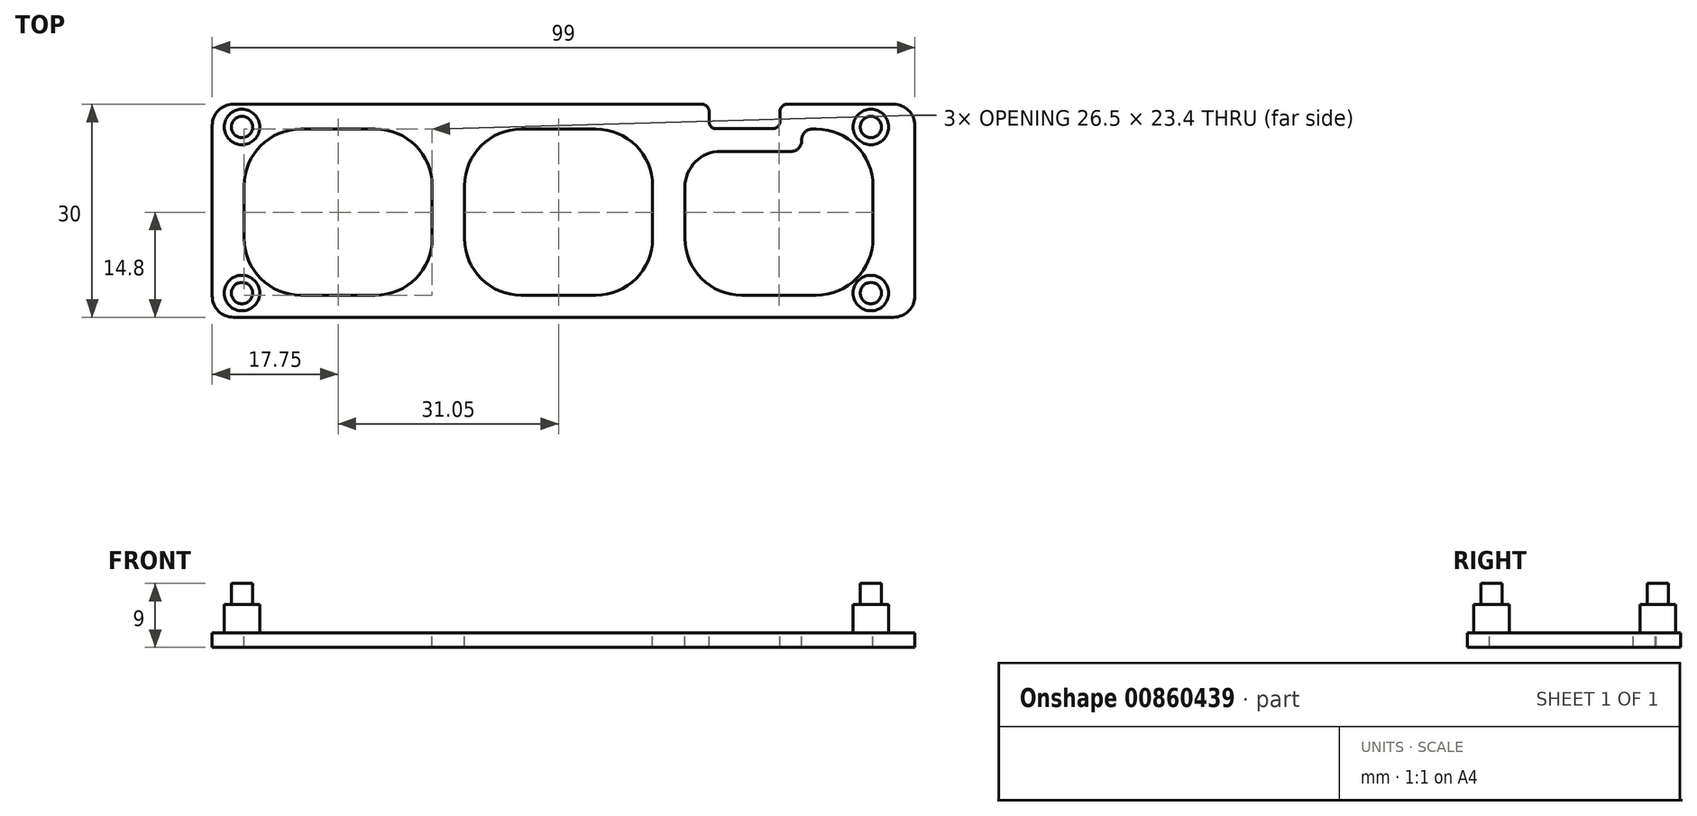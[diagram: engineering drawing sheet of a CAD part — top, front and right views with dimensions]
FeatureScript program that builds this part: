
annotation { "Feature Type Name" : "Feature", "Feature Type Description" : "" }
export const myFeature = defineFeature(function(context is Context, id is Id, definition is map)
    precondition{}
    {
        {
            var Q0;
            Q0=qCreatedBy(makeId("Top.planeOp"),FACE);
            var sketch = newSketch(context, id + "F0", { "sketchPlane" : qUnion([Q0])});
            skLineSegment(sketch, "E0.top", {"start": v(70, -3.43) * mm, "end": v(80, -3.43) * mm});
            skLineSegment(sketch, "E0.left", {"start": v(70, 0) * mm, "end": v(70, -3.43) * mm});
            skLineSegment(sketch, "E0.right", {"start": v(80, 0) * mm, "end": v(80, -3.43) * mm});
            skPoint(sketch, "E1.left.start.orphan", {"position": v(0, 0) * mm});
            skLineSegment(sketch, "E2.bottom", {"start": v(0, 0) * mm, "end": v(70, 0) * mm});
            skLineSegment(sketch, "E2.top", {"start": v(0, -30) * mm, "end": v(99, -30) * mm});
            skLineSegment(sketch, "E2.left", {"start": v(0, 0) * mm, "end": v(0, -30) * mm});
            skLineSegment(sketch, "E2.right", {"start": v(99, 0) * mm, "end": v(99, -30) * mm});
            skLineSegment(sketch, "E3.trimOffspring", {"start": v(80, 0) * mm, "end": v(99, 0) * mm});
            skLineSegment(sketch, "E4.bottom", {"start": v(0, 0) * mm, "end": v(4.5, 0) * mm, "construction": true});
            skLineSegment(sketch, "E4.top", {"start": v(0, -3.5) * mm, "end": v(4.5, -3.5) * mm, "construction": true});
            skLineSegment(sketch, "E4.left", {"start": v(0, 0) * mm, "end": v(0, -3.5) * mm, "construction": true});
            skLineSegment(sketch, "E4.right", {"start": v(4.5, 0) * mm, "end": v(4.5, -3.5) * mm, "construction": true});
            skLineSegment(sketch, "E5.bottom", {"start": v(4.5, -3.5) * mm, "end": v(66.6, -3.5) * mm, "construction": true});
            skLineSegment(sketch, "E5.top", {"start": v(4.5, -26.9) * mm, "end": v(93.1, -26.9) * mm, "construction": true});
            skLineSegment(sketch, "E5.left", {"start": v(4.5, -3.5) * mm, "end": v(4.5, -26.9) * mm, "construction": true});
            skLineSegment(sketch, "E5.right", {"start": v(93.1, -3.5) * mm, "end": v(93.1, -26.9) * mm, "construction": true});
            skLineSegment(sketch, "E6.bottom", {"start": v(12.5, -3.5) * mm, "end": v(23, -3.5) * mm});
            skLineSegment(sketch, "E6.top", {"start": v(12.5, -26.9) * mm, "end": v(23, -26.9) * mm});
            skLineSegment(sketch, "E6.left", {"start": v(4.5, -11.5) * mm, "end": v(4.5, -18.9) * mm});
            skLineSegment(sketch, "E6.right", {"start": v(31, -11.5) * mm, "end": v(31, -18.9) * mm});
            skLineSegment(sketch, "E7.bottom", {"start": v(85.1, -3.5) * mm, "end": v(84.55, -3.5) * mm});
            skLineSegment(sketch, "E7.top", {"start": v(85.1, -26.9) * mm, "end": v(74.6, -26.9) * mm});
            skLineSegment(sketch, "E7.left", {"start": v(93.1, -11.5) * mm, "end": v(93.1, -18.9) * mm});
            skLineSegment(sketch, "E7.right", {"start": v(66.6, -11.65) * mm, "end": v(66.6, -18.9) * mm});
            skLineSegment(sketch, "E8.bottom", {"start": v(43.55, -3.5) * mm, "end": v(54.05, -3.5) * mm});
            skLineSegment(sketch, "E8.top", {"start": v(43.55, -26.9) * mm, "end": v(54.05, -26.9) * mm});
            skLineSegment(sketch, "E8.left", {"start": v(35.55, -11.5) * mm, "end": v(35.55, -18.9) * mm});
            skLineSegment(sketch, "E8.right", {"start": v(62.05, -11.5) * mm, "end": v(62.05, -18.9) * mm});
            skLineSegment(sketch, "E9", {"start": v(4.5, -15.2) * mm, "end": v(31, -15.2) * mm, "construction": true});
            skLineSegment(sketch, "E10", {"start": v(66.6, -15.2) * mm, "end": v(93.1, -15.2) * mm, "construction": true});
            skLineSegment(sketch, "E11", {"start": v(31, -15.2) * mm, "end": v(35.55, -15.2) * mm, "construction": true});
            skLineSegment(sketch, "E12", {"start": v(35.55, -15.2) * mm, "end": v(62.05, -15.2) * mm, "construction": true});
            skLineSegment(sketch, "E13", {"start": v(62.05, -15.2) * mm, "end": v(66.6, -15.2) * mm, "construction": true});
            skLineSegment(sketch, "E14.top", {"start": v(71.6, -6.65) * mm, "end": v(81.55, -6.65) * mm});
            skLineSegment(sketch, "E14.right", {"start": v(83.05, -5) * mm, "end": v(83.05, -5.15) * mm});
            skLineSegment(sketch, "E15.trimOffspring", {"start": v(83.05, -3.5) * mm, "end": v(93.1, -3.5) * mm, "construction": true});
            skPoint(sketch, "E16.visualSharp", {"position": v(4.5, -3.5) * mm});
            skArc(sketch, "E16.filletArc", {"start": v(12.5, -3.5) * mm, "mid": v(6.84, -5.84) * mm, "end": v(4.5, -11.5) * mm});
            skPoint(sketch, "E17.visualSharp", {"position": v(4.5, -26.9) * mm});
            skArc(sketch, "E17.filletArc", {"start": v(4.5, -18.9) * mm, "mid": v(6.84, -24.56) * mm, "end": v(12.5, -26.9) * mm});
            skPoint(sketch, "E18.visualSharp", {"position": v(31, -26.9) * mm});
            skArc(sketch, "E18.filletArc", {"start": v(23, -26.9) * mm, "mid": v(28.66, -24.56) * mm, "end": v(31, -18.9) * mm});
            skPoint(sketch, "E19.visualSharp", {"position": v(31, -3.5) * mm});
            skArc(sketch, "E19.filletArc", {"start": v(31, -11.5) * mm, "mid": v(28.66, -5.84) * mm, "end": v(23, -3.5) * mm});
            skPoint(sketch, "E20.visualSharp", {"position": v(35.55, -26.9) * mm});
            skArc(sketch, "E20.filletArc", {"start": v(35.55, -18.9) * mm, "mid": v(37.9, -24.56) * mm, "end": v(43.55, -26.9) * mm});
            skPoint(sketch, "E21.visualSharp", {"position": v(62.05, -3.5) * mm});
            skArc(sketch, "E21.filletArc", {"start": v(62.05, -11.5) * mm, "mid": v(59.7, -5.84) * mm, "end": v(54.05, -3.5) * mm});
            skPoint(sketch, "E22.visualSharp", {"position": v(62.05, -26.9) * mm});
            skArc(sketch, "E22.filletArc", {"start": v(54.05, -26.9) * mm, "mid": v(59.7, -24.56) * mm, "end": v(62.05, -18.9) * mm});
            skPoint(sketch, "E23.visualSharp", {"position": v(66.6, -26.9) * mm});
            skArc(sketch, "E23.filletArc", {"start": v(66.6, -18.9) * mm, "mid": v(68.94, -24.56) * mm, "end": v(74.6, -26.9) * mm});
            skPoint(sketch, "E24.visualSharp", {"position": v(93.1, -26.9) * mm});
            skArc(sketch, "E24.filletArc", {"start": v(85.1, -26.9) * mm, "mid": v(90.76, -24.56) * mm, "end": v(93.1, -18.9) * mm});
            skPoint(sketch, "E25.visualSharp", {"position": v(93.1, -3.5) * mm});
            skArc(sketch, "E25.filletArc", {"start": v(93.1, -11.5) * mm, "mid": v(90.76, -5.84) * mm, "end": v(85.1, -3.5) * mm});
            skPoint(sketch, "E26.visualSharp", {"position": v(35.55, -3.5) * mm});
            skArc(sketch, "E26.filletArc", {"start": v(43.55, -3.5) * mm, "mid": v(37.9, -5.84) * mm, "end": v(35.55, -11.5) * mm});
            skPoint(sketch, "E27.visualSharp", {"position": v(66.6, -6.65) * mm});
            skArc(sketch, "E27.filletArc", {"start": v(71.6, -6.65) * mm, "mid": v(68.06, -8.11) * mm, "end": v(66.6, -11.65) * mm});
            skPoint(sketch, "E28.visualSharp", {"position": v(83.05, -3.5) * mm});
            skArc(sketch, "E28.filletArc", {"start": v(84.55, -3.5) * mm, "mid": v(83.49, -3.94) * mm, "end": v(83.05, -5) * mm});
            skPoint(sketch, "E29.visualSharp", {"position": v(83.05, -6.65) * mm});
            skArc(sketch, "E29.filletArc", {"start": v(81.55, -6.65) * mm, "mid": v(82.6, -6.2) * mm, "end": v(83.05, -5.15) * mm});
            skSolve(sketch);
        }
        {
            var Q0;
            Q0 = qSketchRegion(id + "F0", true);
            extrude(context, id + "F1", {"entities" : qUnion([Q0]), "depth" : -2 * mm, "offsetDistance" : 25 * mm});
        }
        {
            var Q0;
            Q0=makeQuery(id+"F1.opExtrude","CAP_FACE",FACE,{"disambiguationData":[OSD([sQuery(id+"F0.wireOp",EDGE,"E0.top"),sQuery(id+"F0.wireOp",EDGE,"E0.left"),sQuery(id+"F0.wireOp",EDGE,"E0.right"),sQuery(id+"F0.wireOp",EDGE,"E2.bottom"),sQuery(id+"F0.wireOp",EDGE,"E2.top"),sQuery(id+"F0.wireOp",EDGE,"E2.left"),sQuery(id+"F0.wireOp",EDGE,"E2.right"),sQuery(id+"F0.wireOp",EDGE,"E3.trimOffspring")])],"isStart":true});
            var sketch = newSketch(context, id + "F2", { "sketchPlane" : qUnion([Q0])});
            skLineSegment(sketch, "E30.bottom", {"start": v(4.2, 0) * mm, "end": v(0, 0) * mm, "construction": true});
            skLineSegment(sketch, "E30.top", {"start": v(4.2, -3.2) * mm, "end": v(0, -3.2) * mm, "construction": true});
            skLineSegment(sketch, "E30.left", {"start": v(0, 0) * mm, "end": v(0, -3.2) * mm, "construction": true});
            skLineSegment(sketch, "E30.right", {"start": v(4.2, 0) * mm, "end": v(4.2, -3.2) * mm, "construction": true});
            skCircle(sketch, "E31", {"center": v(4.2, -3.2) * mm, "radius": 2.5 * mm});
            skLineSegment(sketch, "E32.bottom", {"start": v(4.2, -3.2) * mm, "end": v(92.8, -3.2) * mm, "construction": true});
            skLineSegment(sketch, "E32.top", {"start": v(4.2, -26.6) * mm, "end": v(92.8, -26.6) * mm, "construction": true});
            skLineSegment(sketch, "E32.left", {"start": v(4.2, -3.2) * mm, "end": v(4.2, -26.6) * mm, "construction": true});
            skLineSegment(sketch, "E32.right", {"start": v(92.8, -3.2) * mm, "end": v(92.8, -26.6) * mm, "construction": true});
            skCircle(sketch, "E33", {"center": v(92.8, -3.2) * mm, "radius": 2.5 * mm});
            skCircle(sketch, "E34", {"center": v(92.8, -26.6) * mm, "radius": 2.5 * mm});
            skCircle(sketch, "E35", {"center": v(4.2, -26.6) * mm, "radius": 2.5 * mm});
            skCircle(sketch, "E36", {"center": v(4.2, -3.2) * mm, "radius": 1.5 * mm});
            skCircle(sketch, "E37", {"center": v(4.2, -26.6) * mm, "radius": 1.5 * mm});
            skCircle(sketch, "E38", {"center": v(92.8, -26.6) * mm, "radius": 1.5 * mm});
            skCircle(sketch, "E39", {"center": v(92.8, -3.2) * mm, "radius": 1.5 * mm});
            skSolve(sketch);
        }
        {
            var Q0;
            Q0=makeQuery(id+"F1.opExtrude","SWEPT_EDGE",EDGE,{"disambiguationData":[OSD([sQuery(id+"F0.wireOp",EDGE,"IeVyI4JH-hwh0-e2q9-Gude-faWTngmx3L2t.bottom"),sQuery(id+"F0.wireOp",EDGE,"IeVyI4JH-hwh0-e2q9-Gude-faWTngmx3L2t.left")])]});
            var Q1;
            Q1=makeQuery(id+"F1.opExtrude","SWEPT_EDGE",EDGE,{"disambiguationData":[OSD([sQuery(id+"F0.wireOp",EDGE,"ivOO5dQK-mTmG-nhkI-BUbk-pGtQ0CLioyQt.bottom"),sQuery(id+"F0.wireOp",EDGE,"ivOO5dQK-mTmG-nhkI-BUbk-pGtQ0CLioyQt.left")])]});
            var Q2;
            {var subQ0=sQuery(id+"F0.wireOp",EDGE,"E2.right");var subQ1=sQuery(id+"F0.wireOp",EDGE,"E2.top");Q2=makeQuery(id+"FLQB25bvFE6ZXDh_1.boolean.opBoolean","MERGE",EDGE,{"derivedFrom":[makeQuery(id+"F1.opExtrude","SWEPT_EDGE",EDGE,{"disambiguationData":[OSD([subQ1,subQ0])]}),makeQuery(id+"FLQB25bvFE6ZXDh_1.opExtrude","SWEPT_EDGE",EDGE,{"disambiguationData":[OSD([subQ1,subQ0])]})]});}
            var Q3;
            {var subQ0=sQuery(id+"F0.wireOp",EDGE,"E3.trimOffspring");var subQ1=sQuery(id+"F0.wireOp",EDGE,"E2.right");Q3=makeQuery(id+"FLQB25bvFE6ZXDh_1.boolean.opBoolean","MERGE",EDGE,{"derivedFrom":[makeQuery(id+"F1.opExtrude","SWEPT_EDGE",EDGE,{"disambiguationData":[OSD([subQ1,subQ0])]}),makeQuery(id+"FLQB25bvFE6ZXDh_1.opExtrude","SWEPT_EDGE",EDGE,{"disambiguationData":[OSD([subQ1,subQ0])]})]});}
            var Q4;
            {var subQ0=sQuery(id+"F0.wireOp",EDGE,"E2.left");var subQ1=sQuery(id+"F0.wireOp",EDGE,"E2.top");Q4=makeQuery(id+"FLQB25bvFE6ZXDh_1.boolean.opBoolean","MERGE",EDGE,{"derivedFrom":[makeQuery(id+"F1.opExtrude","SWEPT_EDGE",EDGE,{"disambiguationData":[OSD([subQ1,subQ0])]}),makeQuery(id+"FLQB25bvFE6ZXDh_1.opExtrude","SWEPT_EDGE",EDGE,{"disambiguationData":[OSD([subQ1,subQ0])]})]});}
            var Q5;
            {var subQ0=sQuery(id+"F0.wireOp",EDGE,"E2.left");var subQ1=sQuery(id+"F0.wireOp",EDGE,"E2.bottom");Q5=makeQuery(id+"FLQB25bvFE6ZXDh_1.boolean.opBoolean","MERGE",EDGE,{"derivedFrom":[makeQuery(id+"F1.opExtrude","SWEPT_EDGE",EDGE,{"disambiguationData":[OSD([subQ1,subQ0])]}),makeQuery(id+"FLQB25bvFE6ZXDh_1.opExtrude","SWEPT_EDGE",EDGE,{"disambiguationData":[OSD([subQ1,subQ0])]})]});}
            fillet(context, id + "F3", {"entities" : qUnion([Q0, Q1, Q2, Q3, Q4, Q5]), "radius" : 3 * mm, "tangentPropagation" : true, "allowEdgeOverflow" : false});
        }
        {
            var Q0;
            Q0=makeQuery(id+"F1.opExtrude","SWEPT_EDGE",EDGE,{"disambiguationData":[OSD([sQuery(id+"F0.wireOp",EDGE,"IeVyI4JH-hwh0-e2q9-Gude-faWTngmx3L2t.bottom"),sQuery(id+"F0.wireOp",EDGE,"E0.left")])]});
            var Q1;
            Q1=makeQuery(id+"F1.opExtrude","SWEPT_EDGE",EDGE,{"disambiguationData":[OSD([sQuery(id+"F0.wireOp",EDGE,"E0.right"),sQuery(id+"F0.wireOp",EDGE,"c88ff89b-a632-469e-be8a-6d2038dd2af5.trimOffspring")])]});
            var Q2;
            Q2=makeQuery(id+"F1.opExtrude","SWEPT_EDGE",EDGE,{"disambiguationData":[OSD([sQuery(id+"F0.wireOp",EDGE,"E0.top"),sQuery(id+"F0.wireOp",EDGE,"E0.left")])]});
            var Q3;
            Q3=makeQuery(id+"F1.opExtrude","SWEPT_EDGE",EDGE,{"disambiguationData":[OSD([sQuery(id+"F0.wireOp",EDGE,"E0.top"),sQuery(id+"F0.wireOp",EDGE,"E0.right")])]});
            fillet(context, id + "F4", {"entities" : qUnion([Q0, Q1, Q2, Q3]), "radius" : 1 * mm, "tangentPropagation" : true, "allowEdgeOverflow" : false});
        }
        {
            var Q0;
            Q0 = qSketchRegion(id + "F2", true);
            extrude(context, id + "F5", {"entities" : qUnion([Q0]), "operationType" : NewBodyOperationType.ADD, "depth" : 4 * mm, "offsetDistance" : 25 * mm});
        }
        {
            var Q0;
            Q0=makeQuery(id+"F5.boolean.opBoolean","SPLIT",FACE,{"disambiguationData":[TD([makeQuery(id+"F5.opExtrude","SWEPT_FACE",FACE,{"disambiguationData":[OSD([sQuery(id+"F2.wireOp",EDGE,"E36")])]})])],"derivedFrom":makeQuery(id+"F1.opExtrude","CAP_FACE",FACE,{"disambiguationData":[OSD([sQuery(id+"F0.wireOp",EDGE,"E0.top"),sQuery(id+"F0.wireOp",EDGE,"E0.left"),sQuery(id+"F0.wireOp",EDGE,"E0.right"),sQuery(id+"F0.wireOp",EDGE,"E2.bottom"),sQuery(id+"F0.wireOp",EDGE,"E2.top"),sQuery(id+"F0.wireOp",EDGE,"E2.left"),sQuery(id+"F0.wireOp",EDGE,"E2.right"),sQuery(id+"F0.wireOp",EDGE,"E3.trimOffspring")])],"isStart":true})});
            var Q1;
            Q1=makeQuery(id+"F5.boolean.opBoolean","SPLIT",FACE,{"disambiguationData":[TD([makeQuery(id+"F5.opExtrude","SWEPT_FACE",FACE,{"disambiguationData":[OSD([sQuery(id+"F2.wireOp",EDGE,"E37")])]})])],"derivedFrom":makeQuery(id+"F1.opExtrude","CAP_FACE",FACE,{"disambiguationData":[OSD([sQuery(id+"F0.wireOp",EDGE,"E0.top"),sQuery(id+"F0.wireOp",EDGE,"E0.left"),sQuery(id+"F0.wireOp",EDGE,"E0.right"),sQuery(id+"F0.wireOp",EDGE,"E2.bottom"),sQuery(id+"F0.wireOp",EDGE,"E2.top"),sQuery(id+"F0.wireOp",EDGE,"E2.left"),sQuery(id+"F0.wireOp",EDGE,"E2.right"),sQuery(id+"F0.wireOp",EDGE,"E3.trimOffspring")])],"isStart":true})});
            var Q2;
            Q2=makeQuery(id+"F5.boolean.opBoolean","SPLIT",FACE,{"disambiguationData":[TD([makeQuery(id+"F5.opExtrude","SWEPT_FACE",FACE,{"disambiguationData":[OSD([sQuery(id+"F2.wireOp",EDGE,"E39")])]})])],"derivedFrom":makeQuery(id+"F1.opExtrude","CAP_FACE",FACE,{"disambiguationData":[OSD([sQuery(id+"F0.wireOp",EDGE,"E0.top"),sQuery(id+"F0.wireOp",EDGE,"E0.left"),sQuery(id+"F0.wireOp",EDGE,"E0.right"),sQuery(id+"F0.wireOp",EDGE,"E2.bottom"),sQuery(id+"F0.wireOp",EDGE,"E2.top"),sQuery(id+"F0.wireOp",EDGE,"E2.left"),sQuery(id+"F0.wireOp",EDGE,"E2.right"),sQuery(id+"F0.wireOp",EDGE,"E3.trimOffspring")])],"isStart":true})});
            var Q3;
            Q3=makeQuery(id+"F5.boolean.opBoolean","SPLIT",FACE,{"disambiguationData":[TD([makeQuery(id+"F5.opExtrude","SWEPT_FACE",FACE,{"disambiguationData":[OSD([sQuery(id+"F2.wireOp",EDGE,"E38")])]})])],"derivedFrom":makeQuery(id+"F1.opExtrude","CAP_FACE",FACE,{"disambiguationData":[OSD([sQuery(id+"F0.wireOp",EDGE,"E0.top"),sQuery(id+"F0.wireOp",EDGE,"E0.left"),sQuery(id+"F0.wireOp",EDGE,"E0.right"),sQuery(id+"F0.wireOp",EDGE,"E2.bottom"),sQuery(id+"F0.wireOp",EDGE,"E2.top"),sQuery(id+"F0.wireOp",EDGE,"E2.left"),sQuery(id+"F0.wireOp",EDGE,"E2.right"),sQuery(id+"F0.wireOp",EDGE,"E3.trimOffspring")])],"isStart":true})});
            extrude(context, id + "F6", {"entities" : qUnion([Q0, Q1, Q2, Q3]), "operationType" : NewBodyOperationType.ADD, "depth" : 7 * mm, "offsetDistance" : 25 * mm});
        }
    });
